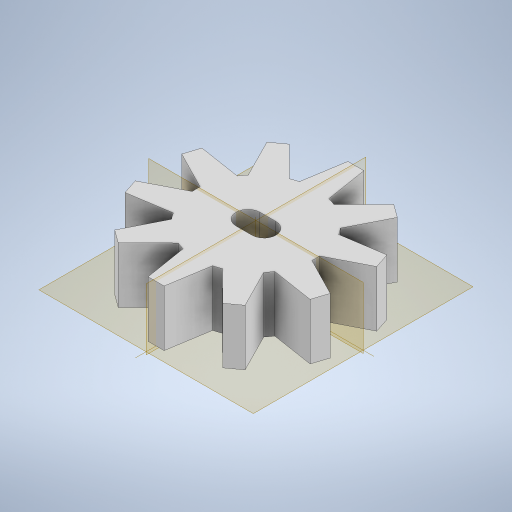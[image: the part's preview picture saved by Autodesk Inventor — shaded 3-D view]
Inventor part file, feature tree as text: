
AUTODESK INVENTOR PART (.ipt)
format: ipt  version: 2023 (Build 270158000, 158)  size: 307,200 bytes
history: native  units: in
note: dims shown in document units (in); Inventor stores cm internally (conversion verified against a paired STEP export)
features: extrude x3, sketch x3
ambient origin geometry x8: Origin, YZ Plane, XZ Plane, XY Plane, X Axis, Y Axis, Z Axis, Center Point
bodies: Solid1 (feature_tree)
feature tree (6):
  extrude  "Extrusion1"  Depth=0.2756in TaperAngle=0.0deg
  extrude  "Extrusion2"  Depth=0.1969in
  extrude  "Extrusion3"  Depth=0.2756in TaperAngle=0.0deg
  sketch  "Sketch1"  dims[d0=0.5906in d1=0.2756in d2=0.0in]
  sketch  "Sketch2"  dims[d3=0.0984in d4=0.1969in]
  sketch  "Sketch3"  dims[d5=0.1181in d6=0.2756in d7=0.0in d9=0.0394in d10=3.937in d12=360.0deg d14=0.2756in d15=0.0in]
